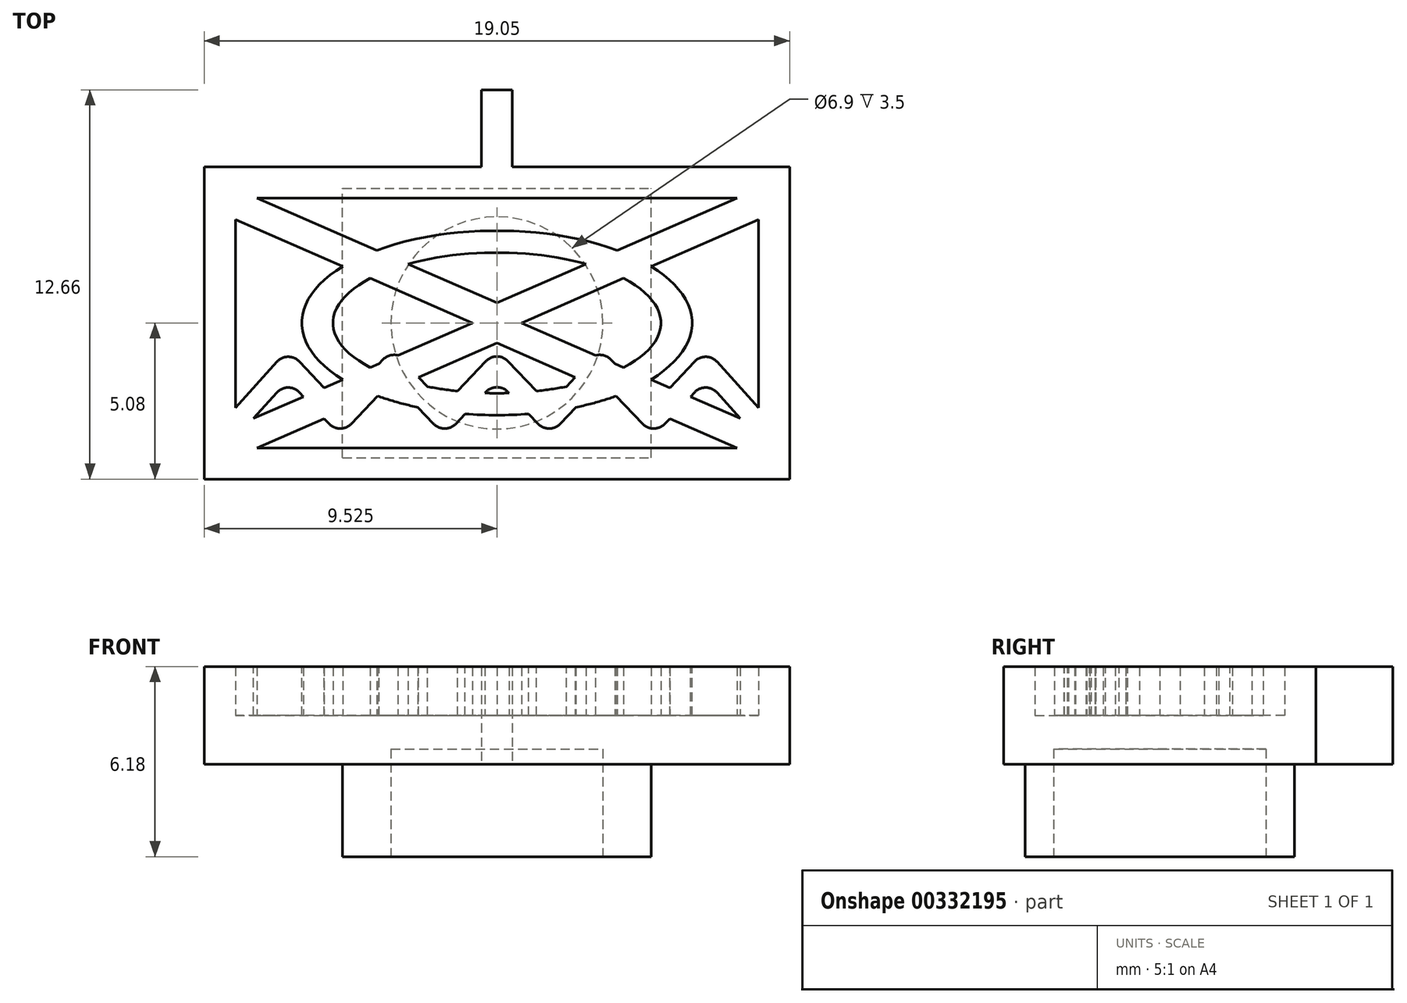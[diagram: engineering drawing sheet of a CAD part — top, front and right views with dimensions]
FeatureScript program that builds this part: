
annotation { "Feature Type Name" : "Feature", "Feature Type Description" : "" }
export const myFeature = defineFeature(function(context is Context, id is Id, definition is map)
    precondition{}
    {
        {
            var Q0;
            Q0=qCreatedBy(makeId("Top.planeOp"),FACE);
            var sketch = newSketch(context, id + "F0", { "sketchPlane" : qUnion([Q0])});
            skLineSegment(sketch, "E0.bottom", {"start": v(-19.05, 10.16) * mm, "end": v(0, 10.16) * mm});
            skLineSegment(sketch, "E0.top", {"start": v(-19.05, 0) * mm, "end": v(0, 0) * mm});
            skLineSegment(sketch, "E0.left", {"start": v(-19.05, 10.16) * mm, "end": v(-19.05, 0) * mm});
            skLineSegment(sketch, "E0.right", {"start": v(0, 10.16) * mm, "end": v(0, 0) * mm});
            skLineSegment(sketch, "E1", {"start": v(-9.52, 10.16) * mm, "end": v(-9.52, 0) * mm, "construction": true});
            skLineSegment(sketch, "E2.bottom", {"start": v(-10.02, 12.66) * mm, "end": v(-9.02, 12.66) * mm});
            skLineSegment(sketch, "E2.top", {"start": v(-10.02, 10.16) * mm, "end": v(-9.02, 10.16) * mm});
            skLineSegment(sketch, "E2.left", {"start": v(-10.02, 12.66) * mm, "end": v(-10.02, 10.16) * mm});
            skLineSegment(sketch, "E2.right", {"start": v(-9.02, 12.66) * mm, "end": v(-9.02, 10.16) * mm});
            skSolve(sketch);
        }
        {
            var Q0;
            Q0=qSketchRegion(id+"F0",true);
            extrude(context, id + "F1", {"entities" : qUnion([Q0]), "depth" : 3.17 * mm});
        }
        {
            var Q0;
            Q0=makeQuery(id+"F1.opExtrude","CAP_FACE",FACE,{"disambiguationData":[OSD([sQuery(id+"F0.wireOp",EDGE,"E0.bottom"),sQuery(id+"F0.wireOp",EDGE,"E0.top"),sQuery(id+"F0.wireOp",EDGE,"E0.left"),sQuery(id+"F0.wireOp",EDGE,"E0.right")])],"isStart":false});
            var sketch = newSketch(context, id + "F2", { "sketchPlane" : qUnion([Q0])});
            skLineSegment(sketch, "E3.bottom", {"start": v(-18.03, 9.14) * mm, "end": v(-1.02, 9.14) * mm});
            skLineSegment(sketch, "E3.top", {"start": v(-18.03, 1.02) * mm, "end": v(-1.02, 1.02) * mm});
            skLineSegment(sketch, "E3.left", {"start": v(-18.03, 9.14) * mm, "end": v(-18.03, 1.02) * mm});
            skLineSegment(sketch, "E3.right", {"start": v(-1.02, 9.14) * mm, "end": v(-1.02, 1.02) * mm});
            skSolve(sketch);
        }
        {
            var Q0;
            Q0=qSketchRegion(id+"F2",true);
            extrude(context, id + "F3", {"entities" : qUnion([Q0]), "operationType" : NewBodyOperationType.REMOVE, "oppositeDirection" : true, "depth" : 1.59 * mm});
        }
        {
            var Q0;
            {var subQ0=sQuery(id+"F2.wireOp",EDGE,"E3.bottom");var subQ1=sQuery(id+"F2.wireOp",EDGE,"E3.left");Q0=makeQuery(id+"FD6hazfNaiJcgqe_1.boolean.opBoolean","SPLIT",FACE,{"disambiguationData":[TD([makeQuery(id+"F3.boolean.opBoolean","COPY",FACE,{"derivedFrom":makeQuery(id+"F3.opExtrude","SWEPT_FACE",FACE,{"disambiguationData":[OSD([subQ0])]})})])],"derivedFrom":makeQuery(id+"F3.boolean.opBoolean","COPY",FACE,{"derivedFrom":makeQuery(id+"F3.opExtrude","CAP_FACE",FACE,{"disambiguationData":[OSD([subQ0,sQuery(id+"F2.wireOp",EDGE,"E3.top"),subQ1,sQuery(id+"F2.wireOp",EDGE,"E3.right")])],"isStart":false})})});}
            var sketch = newSketch(context, id + "F4", { "sketchPlane" : qUnion([Q0])});
            skLineSegment(sketch, "E4", {"start": v(-9.52, 10.16) * mm, "end": v(-9.52, 0) * mm, "construction": true});
            skLineSegment(sketch, "E5", {"start": v(-19.05, 5.08) * mm, "end": v(0, 5.08) * mm, "construction": true});
            skEllipse(sketch, "E6", {"center": v(-9.52, 5.08) * mm, "majorRadius": 5.33 * mm, "minorRadius": 2.29 * mm, "majorAxis": v(-1, 0)});
            skEllipse(sketch, "E7", {"center": v(-9.52, 5.08) * mm, "majorRadius": 6.35 * mm, "minorRadius": 3 * mm, "majorAxis": v(1, 0)});
            skSolve(sketch);
        }
        {
            var Q0;
            Q0=qSketchRegion(id+"F4",true);
            var Q1;
            Q1=makeQuery(id+"FD6hazfNaiJcgqe_1.boolean.opBoolean","MERGE",FACE,{"derivedFrom":[makeQuery(id+"F1.opExtrude","CAP_FACE",FACE,{"disambiguationData":[OSD([sQuery(id+"F0.wireOp",EDGE,"E0.bottom"),sQuery(id+"F0.wireOp",EDGE,"E0.top"),sQuery(id+"F0.wireOp",EDGE,"E0.left"),sQuery(id+"F0.wireOp",EDGE,"E0.right"),sQuery(id+"F0.wireOp",EDGE,"XctMcTzM-jzK6-gSmv-2nxO-Hmrl2WoydrkH.bottom"),sQuery(id+"F0.wireOp",EDGE,"XctMcTzM-jzK6-gSmv-2nxO-Hmrl2WoydrkH.left"),sQuery(id+"F0.wireOp",EDGE,"XctMcTzM-jzK6-gSmv-2nxO-Hmrl2WoydrkH.right")])],"isStart":false}),makeQuery(id+"FD6hazfNaiJcgqe_1.opExtrude","CAP_FACE",FACE,{"disambiguationData":[OSD([sQuery(id+"FBnKpMS2cNLFyNX_1.wireOp",EDGE,"OeS0QawB-iup7-bIXq-nBgO-fnigf9KOmNtt"),sQuery(id+"FBnKpMS2cNLFyNX_1.wireOp",EDGE,"xYslIAmR-IU4A-U8Ev-eRzx-1tLUXoU8zJ8x"),sQuery(id+"FBnKpMS2cNLFyNX_1.wireOp",EDGE,"s2yYm8nE-9nAX-yXiD-gElo-VwSO6LMNS3os"),sQuery(id+"FBnKpMS2cNLFyNX_1.wireOp",EDGE,"BWi2MzMB-bow1-vDxn-7ShQ-1YiDBgTSlN10"),sQuery(id+"FBnKpMS2cNLFyNX_1.wireOp",EDGE,"4fcJUz5v-7g5D-GTkM-eBk7-cmIldQICNH6a"),sQuery(id+"FBnKpMS2cNLFyNX_1.wireOp",EDGE,"JyWkrWma-j76y-q2y8-kGDN-Km0VDhZBhLyh"),sQuery(id+"FBnKpMS2cNLFyNX_1.wireOp",EDGE,"hH4EWFfC-tNwj-oGm0-8eoL-p1ctc8BhzRw8"),sQuery(id+"FBnKpMS2cNLFyNX_1.wireOp",EDGE,"unhDRoPr-LBfY-NyqK-AVhX-2gFjzCdnZd3x"),sQuery(id+"FBnKpMS2cNLFyNX_1.wireOp",EDGE,"eioCPEry-a7AL-AyuY-AUbQ-wWZvTsCijl4n"),sQuery(id+"FBnKpMS2cNLFyNX_1.wireOp",EDGE,"ga3sPcsW-uslI-afVP-5EuA-U3aNN3MUd2xP"),sQuery(id+"FBnKpMS2cNLFyNX_1.wireOp",EDGE,"2eZ3HgfS-F6HE-pDFD-BtrP-3SBC7ZAuQREh"),sQuery(id+"FBnKpMS2cNLFyNX_1.wireOp",EDGE,"egwDE0gL-gJxL-a5VO-DP01-p7e11LL6TNIh"),sQuery(id+"FBnKpMS2cNLFyNX_1.wireOp",EDGE,"Oc6yrfE5-Wmlw-YOVM-BoAX-kQYr9RLupFyV"),sQuery(id+"FBnKpMS2cNLFyNX_1.wireOp",EDGE,"HKjVjBGv-TE9a-NIGQ-HE8n-yFD3IG2zp62e")])],"isStart":false})]});
            extrude(context, id + "F5", {"entities" : qUnion([Q0]), "operationType" : NewBodyOperationType.ADD, "endBound" : BoundingType.UP_TO_SURFACE, "endBoundEntityFace" : qUnion([Q1]), "depth" : 25.4 * mm});
        }
        {
            var Q0;
            {var subQ1=sQuery(id+"F2.wireOp",EDGE,"E3.top");var subQ4=makeQuery(id+"F3.boolean.opBoolean","COPY",FACE,{"derivedFrom":makeQuery(id+"F3.opExtrude","SWEPT_FACE",FACE,{"disambiguationData":[OSD([subQ1])]})});var subQ6=sQuery(id+"F2.wireOp",EDGE,"E3.right");Q0=makeQuery(id+"F5.boolean.opBoolean","SPLIT",FACE,{"disambiguationData":[TD([subQ4])],"derivedFrom":makeQuery(id+"FD6hazfNaiJcgqe_1.boolean.opBoolean","SPLIT",FACE,{"disambiguationData":[TD([subQ4])],"derivedFrom":makeQuery(id+"F3.boolean.opBoolean","COPY",FACE,{"derivedFrom":makeQuery(id+"F3.opExtrude","CAP_FACE",FACE,{"disambiguationData":[OSD([sQuery(id+"F2.wireOp",EDGE,"E3.bottom"),subQ1,sQuery(id+"F2.wireOp",EDGE,"E3.left"),subQ6])],"isStart":false})})})});}
            var sketch = newSketch(context, id + "F6", { "sketchPlane" : qUnion([Q0])});
            skLineSegment(sketch, "E8", {"start": v(-19.05, 1.68) * mm, "end": v(-1.02, 1.68) * mm, "construction": true});
            skLineSegment(sketch, "E9", {"start": v(-9.53, 10.16) * mm, "end": v(-9.53, 0) * mm, "construction": true});
            skSolve(sketch);
        }
        {
            var Q0;
            Q0=makeQuery(id+"F1.opExtrude","CAP_FACE",FACE,{"disambiguationData":[OSD([sQuery(id+"F0.wireOp",EDGE,"E0.bottom"),sQuery(id+"F0.wireOp",EDGE,"E0.top"),sQuery(id+"F0.wireOp",EDGE,"E0.left"),sQuery(id+"F0.wireOp",EDGE,"E0.right"),sQuery(id+"F0.wireOp",EDGE,"iD4YVwzi-38ZZ-sZow-cuPB-LK5aPxXRs2tg"),sQuery(id+"F0.wireOp",EDGE,"25aa8db4-dd9b-41d2-b8c9-1594e9b75191"),sQuery(id+"F0.wireOp",EDGE,"40f63cb3-13d8-4821-a3c4-c05e674bd89b0.MirrorC")])],"isStart":true});
            var sketch = newSketch(context, id + "F7", { "sketchPlane" : qUnion([Q0])});
            skLineSegment(sketch, "E10.bottom", {"start": v(-14.55, -0.7) * mm, "end": v(-4.5, -0.7) * mm});
            skLineSegment(sketch, "E10.top", {"start": v(-14.55, -9.46) * mm, "end": v(-4.5, -9.46) * mm});
            skLineSegment(sketch, "E10.left", {"start": v(-14.55, -0.7) * mm, "end": v(-14.55, -9.46) * mm});
            skLineSegment(sketch, "E10.right", {"start": v(-4.5, -0.7) * mm, "end": v(-4.5, -9.46) * mm});
            skSolve(sketch);
        }
        {
            var Q0;
            Q0=qSketchRegion(id+"F7",true);
            extrude(context, id + "F8", {"entities" : qUnion([Q0]), "operationType" : NewBodyOperationType.ADD, "depth" : 3 * mm, "offsetDistance" : 25 * mm});
        }
        {
            var Q0;
            Q0=makeQuery(id+"F8.opExtrude","CAP_FACE",FACE,{"disambiguationData":[OSD([sQuery(id+"F7.wireOp",EDGE,"E10.bottom"),sQuery(id+"F7.wireOp",EDGE,"E10.top"),sQuery(id+"F7.wireOp",EDGE,"E10.left"),sQuery(id+"F7.wireOp",EDGE,"E10.right")])],"isStart":false});
            var sketch = newSketch(context, id + "F9", { "sketchPlane" : qUnion([Q0])});
            skCircle(sketch, "E11", {"center": v(-9.52, -5.08) * mm, "radius": 3.45 * mm});
            skLineSegment(sketch, "E12", {"start": v(-19.05, -5.08) * mm, "end": v(0, -5.08) * mm, "construction": true});
            skPoint(sketch, "E12.endSnap0", {"position": v(-4.5, -5.08) * mm});
            skLineSegment(sketch, "E13", {"start": v(-9.53, 0) * mm, "end": v(-9.53, -9.46) * mm, "construction": true});
            skSolve(sketch);
        }
        {
            var Q0;
            Q0=makeQuery(id+"F9.imprint","IMPRINT",FACE,{"disambiguationData":[TD([[makeQuery(id+"F9.imprint","IMPRINT",EDGE,{"derivedFrom":sQuery(id+"F9.wireOp",EDGE,"E11")}),1.0]])]});
            extrude(context, id + "F10", {"entities" : qUnion([Q0]), "operationType" : NewBodyOperationType.REMOVE, "oppositeDirection" : true, "depth" : 3.5 * mm, "offsetDistance" : 25 * mm});
        }
        {
            var Q0;
            Q0=makeQuery(id+"F6.imprint","IMPRINT",FACE,{"disambiguationData":[TD([[makeQuery(id+"F6.imprint","IMPRINT",EDGE,{"derivedFrom":makeQuery(id+"F3.boolean.opBoolean","COPY",EDGE,{"derivedFrom":makeQuery(id+"F3.opExtrude","CAP_EDGE",EDGE,{"disambiguationData":[OSD([sQuery(id+"F2.wireOp",EDGE,"E3.bottom")])],"isStart":false})})}),-1.0]])]});
            var sketch = newSketch(context, id + "F11", { "sketchPlane" : qUnion([Q0])});
            skLineSegment(sketch, "E14", {"start": v(-18.03, 2.32) * mm, "end": v(-16.33, 4.22) * mm});
            skLineSegment(sketch, "E15", {"start": v(-16.33, 4.22) * mm, "end": v(-14.63, 2.42) * mm});
            skLineSegment(sketch, "E16", {"start": v(-14.63, 2.42) * mm, "end": v(-12.93, 4.22) * mm});
            skLineSegment(sketch, "E17", {"start": v(-12.93, 4.22) * mm, "end": v(-11.23, 2.42) * mm});
            skLineSegment(sketch, "E18", {"start": v(-11.23, 2.42) * mm, "end": v(-9.53, 4.22) * mm});
            skLineSegment(sketch, "E19", {"start": v(-9.53, 1.02) * mm, "end": v(-9.53, 9.14) * mm, "construction": true});
            skLineSegment(sketch, "E20", {"start": v(-11.23, 9.14) * mm, "end": v(-11.23, 1.02) * mm, "construction": true});
            skLineSegment(sketch, "E21", {"start": v(-12.93, 9.14) * mm, "end": v(-12.93, 1.02) * mm, "construction": true});
            skLineSegment(sketch, "E22", {"start": v(-14.63, 9.14) * mm, "end": v(-14.63, 1.02) * mm, "construction": true});
            skLineSegment(sketch, "E23", {"start": v(-16.33, 9.14) * mm, "end": v(-16.33, 1.02) * mm, "construction": true});
            skLineSegment(sketch, "E24", {"start": v(-18.03, 3.32) * mm, "end": v(-9.53, 3.32) * mm, "construction": true});
            skLineSegment(sketch, "E25", {"start": v(-18.03, 2.32) * mm, "end": v(-18.03, 1.32) * mm});
            skLineSegment(sketch, "E26", {"start": v(-18.03, 1.32) * mm, "end": v(-16.33, 3.22) * mm});
            skLineSegment(sketch, "E27", {"start": v(-16.33, 3.22) * mm, "end": v(-14.63, 1.42) * mm});
            skLineSegment(sketch, "E28", {"start": v(-14.63, 1.42) * mm, "end": v(-12.93, 3.22) * mm});
            skLineSegment(sketch, "E29", {"start": v(-12.93, 3.22) * mm, "end": v(-11.23, 1.42) * mm});
            skLineSegment(sketch, "E30", {"start": v(-11.23, 1.42) * mm, "end": v(-9.53, 3.22) * mm});
            skLineSegment(sketch, "E31.MirrorCS", {"start": v(-7.83, 1.42) * mm, "end": v(-9.53, 3.22) * mm});
            skLineSegment(sketch, "E32.MirrorCS", {"start": v(-7.83, 2.42) * mm, "end": v(-9.53, 4.22) * mm});
            skLineSegment(sketch, "E33.MirrorCS", {"start": v(-6.13, 4.22) * mm, "end": v(-7.83, 2.42) * mm});
            skLineSegment(sketch, "E34.MirrorCS", {"start": v(-6.12, 3.22) * mm, "end": v(-7.83, 1.42) * mm});
            skLineSegment(sketch, "E35.MirrorCS", {"start": v(-4.42, 1.42) * mm, "end": v(-6.12, 3.22) * mm});
            skLineSegment(sketch, "E36.MirrorCS", {"start": v(-4.42, 2.42) * mm, "end": v(-6.12, 4.22) * mm});
            skLineSegment(sketch, "E37.MirrorCS", {"start": v(-2.73, 4.22) * mm, "end": v(-4.42, 2.42) * mm});
            skLineSegment(sketch, "E38.MirrorCS", {"start": v(-2.73, 3.22) * mm, "end": v(-4.42, 1.42) * mm});
            skLineSegment(sketch, "E39.MirrorCS", {"start": v(-1.02, 1.32) * mm, "end": v(-2.73, 3.22) * mm});
            skLineSegment(sketch, "E40.MirrorCS", {"start": v(-1.02, 2.32) * mm, "end": v(-2.73, 4.22) * mm});
            skLineSegment(sketch, "E41.MirrorCS", {"start": v(-1.02, 2.32) * mm, "end": v(-1.02, 1.32) * mm});
            skSolve(sketch);
        }
        {
            var Q0;
            Q0 = qSketchRegion(id + "F11", true);
            var Q1;
            Q1=makeQuery(id+"F5.opExtrude","CAP_FACE",FACE,{"disambiguationData":[OSD([sQuery(id+"F4.wireOp",EDGE,"E6"),sQuery(id+"F4.wireOp",EDGE,"E7")])],"isStart":false});
            extrude(context, id + "F12", {"entities" : qUnion([Q0]), "operationType" : NewBodyOperationType.ADD, "endBound" : BoundingType.UP_TO_SURFACE, "depth" : 25 * mm, "endBoundEntityFace" : qUnion([Q1]), "offsetDistance" : 25 * mm});
        }
        {
            var Q0;
            Q0=makeQuery(id+"F6.imprint","IMPRINT",FACE,{"disambiguationData":[TD([[makeQuery(id+"F6.imprint","IMPRINT",EDGE,{"derivedFrom":makeQuery(id+"F3.boolean.opBoolean","COPY",EDGE,{"derivedFrom":makeQuery(id+"F3.opExtrude","CAP_EDGE",EDGE,{"disambiguationData":[OSD([sQuery(id+"F2.wireOp",EDGE,"E3.bottom")])],"isStart":false})})}),-1.0]])]});
            var sketch = newSketch(context, id + "F13", { "sketchPlane" : qUnion([Q0])});
            skLineSegment(sketch, "E42", {"start": v(-1.72, 9.14) * mm, "end": v(-9.53, 5.74) * mm});
            skLineSegment(sketch, "E43", {"start": v(-8.73, 5.08) * mm, "end": v(-1.02, 8.44) * mm});
            skLineSegment(sketch, "E44", {"start": v(-1.02, 8.44) * mm, "end": v(-1.02, 9.14) * mm});
            skLineSegment(sketch, "E45", {"start": v(-1.02, 9.14) * mm, "end": v(-1.72, 9.14) * mm});
            skLineSegment(sketch, "E46", {"start": v(-19.05, 5.08) * mm, "end": v(0, 5.08) * mm, "construction": true});
            skLineSegment(sketch, "E47.MirrorCS", {"start": v(-17.33, 9.14) * mm, "end": v(-9.53, 5.74) * mm});
            skLineSegment(sketch, "E48.MirrorCS", {"start": v(-10.33, 5.08) * mm, "end": v(-18.03, 8.44) * mm});
            skLineSegment(sketch, "E49.MirrorCS", {"start": v(-18.03, 8.44) * mm, "end": v(-18.03, 9.14) * mm});
            skLineSegment(sketch, "E50.MirrorCS", {"start": v(-18.03, 9.14) * mm, "end": v(-17.33, 9.14) * mm});
            skLineSegment(sketch, "E51.MirrorCS", {"start": v(-10.33, 5.08) * mm, "end": v(-18.03, 1.72) * mm});
            skLineSegment(sketch, "E52.MirrorCS", {"start": v(-8.73, 5.08) * mm, "end": v(-1.02, 1.72) * mm});
            skLineSegment(sketch, "E53.MirrorCS", {"start": v(-1.72, 1.02) * mm, "end": v(-9.53, 4.42) * mm});
            skLineSegment(sketch, "E54.MirrorCS", {"start": v(-17.33, 1.02) * mm, "end": v(-9.53, 4.42) * mm});
            skLineSegment(sketch, "E55.MirrorCS", {"start": v(-18.03, 1.02) * mm, "end": v(-17.33, 1.02) * mm});
            skLineSegment(sketch, "E56.MirrorCS", {"start": v(-18.03, 1.72) * mm, "end": v(-18.03, 1.02) * mm});
            skLineSegment(sketch, "E57.MirrorCS", {"start": v(-1.02, 1.72) * mm, "end": v(-1.02, 1.02) * mm});
            skLineSegment(sketch, "E58.MirrorCS", {"start": v(-1.02, 1.02) * mm, "end": v(-1.72, 1.02) * mm});
            skSolve(sketch);
        }
        {
            var Q0;
            Q0 = qSketchRegion(id + "F13", true);
            var Q1;
            Q1=makeQuery(id+"F12.boolean.opBoolean","MERGE",FACE,{"derivedFrom":[makeQuery(id+"F1.opExtrude","CAP_FACE",FACE,{"disambiguationData":[OSD([sQuery(id+"F0.wireOp",EDGE,"E0.bottom"),sQuery(id+"F0.wireOp",EDGE,"E0.top"),sQuery(id+"F0.wireOp",EDGE,"E0.left"),sQuery(id+"F0.wireOp",EDGE,"E0.right"),sQuery(id+"F0.wireOp",EDGE,"25aa8db4-dd9b-41d2-b8c9-1594e9b75191"),sQuery(id+"F0.wireOp",EDGE,"40f63cb3-13d8-4821-a3c4-c05e674bd89b0.MirrorC")])],"isStart":false}),makeQuery(id+"F5.opExtrude","CAP_FACE",FACE,{"disambiguationData":[OSD([sQuery(id+"F4.wireOp",EDGE,"E6"),sQuery(id+"F4.wireOp",EDGE,"E7")])],"isStart":false}),makeQuery(id+"F12.opExtrude","CAP_FACE",FACE,{"disambiguationData":[OSD([sQuery(id+"F11.wireOp",EDGE,"E14"),sQuery(id+"F11.wireOp",EDGE,"E15"),sQuery(id+"F11.wireOp",EDGE,"E16"),sQuery(id+"F11.wireOp",EDGE,"E17"),sQuery(id+"F11.wireOp",EDGE,"E18"),sQuery(id+"F11.wireOp",EDGE,"E25"),sQuery(id+"F11.wireOp",EDGE,"E26"),sQuery(id+"F11.wireOp",EDGE,"E27"),sQuery(id+"F11.wireOp",EDGE,"E28"),sQuery(id+"F11.wireOp",EDGE,"E29"),sQuery(id+"F11.wireOp",EDGE,"E30"),sQuery(id+"F11.wireOp",EDGE,"E31.MirrorCS"),sQuery(id+"F11.wireOp",EDGE,"E32.MirrorCS"),sQuery(id+"F11.wireOp",EDGE,"E33.MirrorCS"),sQuery(id+"F11.wireOp",EDGE,"E34.MirrorCS"),sQuery(id+"F11.wireOp",EDGE,"E35.MirrorCS"),sQuery(id+"F11.wireOp",EDGE,"E36.MirrorCS"),sQuery(id+"F11.wireOp",EDGE,"E37.MirrorCS"),sQuery(id+"F11.wireOp",EDGE,"E38.MirrorCS"),sQuery(id+"F11.wireOp",EDGE,"E39.MirrorCS"),sQuery(id+"F11.wireOp",EDGE,"E40.MirrorCS"),sQuery(id+"F11.wireOp",EDGE,"E41.MirrorCS")])],"isStart":false})]});
            extrude(context, id + "F14", {"entities" : qUnion([Q0]), "operationType" : NewBodyOperationType.ADD, "endBound" : BoundingType.UP_TO_SURFACE, "depth" : 25 * mm, "endBoundEntityFace" : qUnion([Q1]), "offsetDistance" : 25 * mm});
        }
        {
            var Q0;
            Q0=makeQuery(id+"F12.opExtrude","SWEPT_EDGE",EDGE,{"disambiguationData":[OSD([sQuery(id+"F11.wireOp",EDGE,"E27"),sQuery(id+"F11.wireOp",EDGE,"E28")])]});
            var Q1;
            Q1=makeQuery(id+"F12.opExtrude","SWEPT_EDGE",EDGE,{"disambiguationData":[OSD([sQuery(id+"F11.wireOp",EDGE,"E14"),sQuery(id+"F11.wireOp",EDGE,"E15")])]});
            var Q2;
            Q2=makeQuery(id+"F12.opExtrude","SWEPT_EDGE",EDGE,{"disambiguationData":[OSD([sQuery(id+"F11.wireOp",EDGE,"E35.MirrorCS"),sQuery(id+"F11.wireOp",EDGE,"E38.MirrorCS")])]});
            var Q3;
            Q3=makeQuery(id+"F12.opExtrude","SWEPT_EDGE",EDGE,{"disambiguationData":[OSD([sQuery(id+"F11.wireOp",EDGE,"E31.MirrorCS"),sQuery(id+"F11.wireOp",EDGE,"E34.MirrorCS")])]});
            var Q4;
            Q4=makeQuery(id+"F12.opExtrude","SWEPT_EDGE",EDGE,{"disambiguationData":[OSD([sQuery(id+"F11.wireOp",EDGE,"E29"),sQuery(id+"F11.wireOp",EDGE,"E30")])]});
            var Q5;
            Q5=makeQuery(id+"F12.opExtrude","SWEPT_EDGE",EDGE,{"disambiguationData":[OSD([sQuery(id+"F11.wireOp",EDGE,"E16"),sQuery(id+"F11.wireOp",EDGE,"E17")])]});
            var Q6;
            Q6=makeQuery(id+"F12.opExtrude","SWEPT_EDGE",EDGE,{"disambiguationData":[OSD([sQuery(id+"F11.wireOp",EDGE,"E18"),sQuery(id+"F11.wireOp",EDGE,"E32.MirrorCS")])]});
            var Q7;
            Q7=makeQuery(id+"F12.opExtrude","SWEPT_EDGE",EDGE,{"disambiguationData":[OSD([sQuery(id+"F11.wireOp",EDGE,"E33.MirrorCS"),sQuery(id+"F11.wireOp",EDGE,"E36.MirrorCS")])]});
            var Q8;
            Q8=makeQuery(id+"F12.opExtrude","SWEPT_EDGE",EDGE,{"disambiguationData":[OSD([sQuery(id+"F11.wireOp",EDGE,"E37.MirrorCS"),sQuery(id+"F11.wireOp",EDGE,"E40.MirrorCS")])]});
            var Q9;
            Q9=makeQuery(id+"F12.opExtrude","SWEPT_EDGE",EDGE,{"disambiguationData":[OSD([sQuery(id+"F11.wireOp",EDGE,"E30"),sQuery(id+"F11.wireOp",EDGE,"E31.MirrorCS")])]});
            var Q10;
            Q10=makeQuery(id+"F12.opExtrude","SWEPT_EDGE",EDGE,{"disambiguationData":[OSD([sQuery(id+"F11.wireOp",EDGE,"E38.MirrorCS"),sQuery(id+"F11.wireOp",EDGE,"E39.MirrorCS")])]});
            var Q11;
            Q11=makeQuery(id+"F12.opExtrude","SWEPT_EDGE",EDGE,{"disambiguationData":[OSD([sQuery(id+"F11.wireOp",EDGE,"E26"),sQuery(id+"F11.wireOp",EDGE,"E27")])]});
            fillet(context, id + "F15", {"entities" : qUnion([Q0, Q1, Q2, Q3, Q4, Q5, Q6, Q7, Q8, Q9, Q10, Q11]), "tangentPropagation" : true, "radius" : .5 * mm, "defaultsChanged" : false, "vertexSettings" : [], "allowEdgeOverflow" : false});
        }
    });
